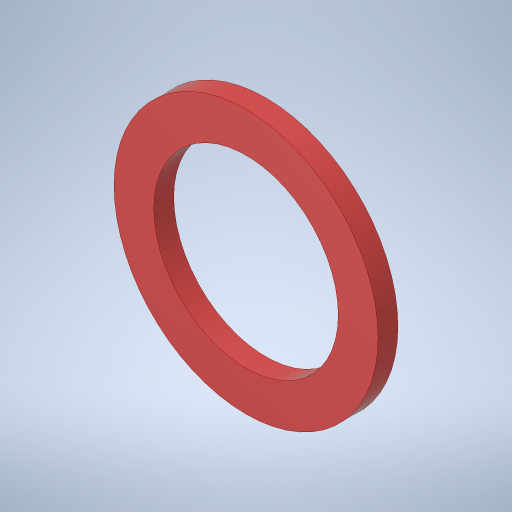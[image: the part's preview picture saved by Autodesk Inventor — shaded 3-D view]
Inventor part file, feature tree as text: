
AUTODESK INVENTOR PART (.ipt)
format: ipt  version: 2023.4 (Build 274418000, 418)  size: 248,832 bytes
history: native  units: in
note: dims shown in document units (in); Inventor stores cm internally (conversion verified against a paired STEP export)
features: extrude x1
ambient origin geometry x8: Origin, YZ Plane, XZ Plane, XY Plane, X Axis, Y Axis, Z Axis, Center Point
bodies: Solid1 (feature_tree)
feature tree (1):
  extrude  "Extrusion1"  TaperAngle=0.0deg  [1 undecoded]
note: 1 required parameter value undecoded (feature->parameter linkage not recoverable at this tier; creation-order binding heuristic only, values carry confidence <= 0.55)
